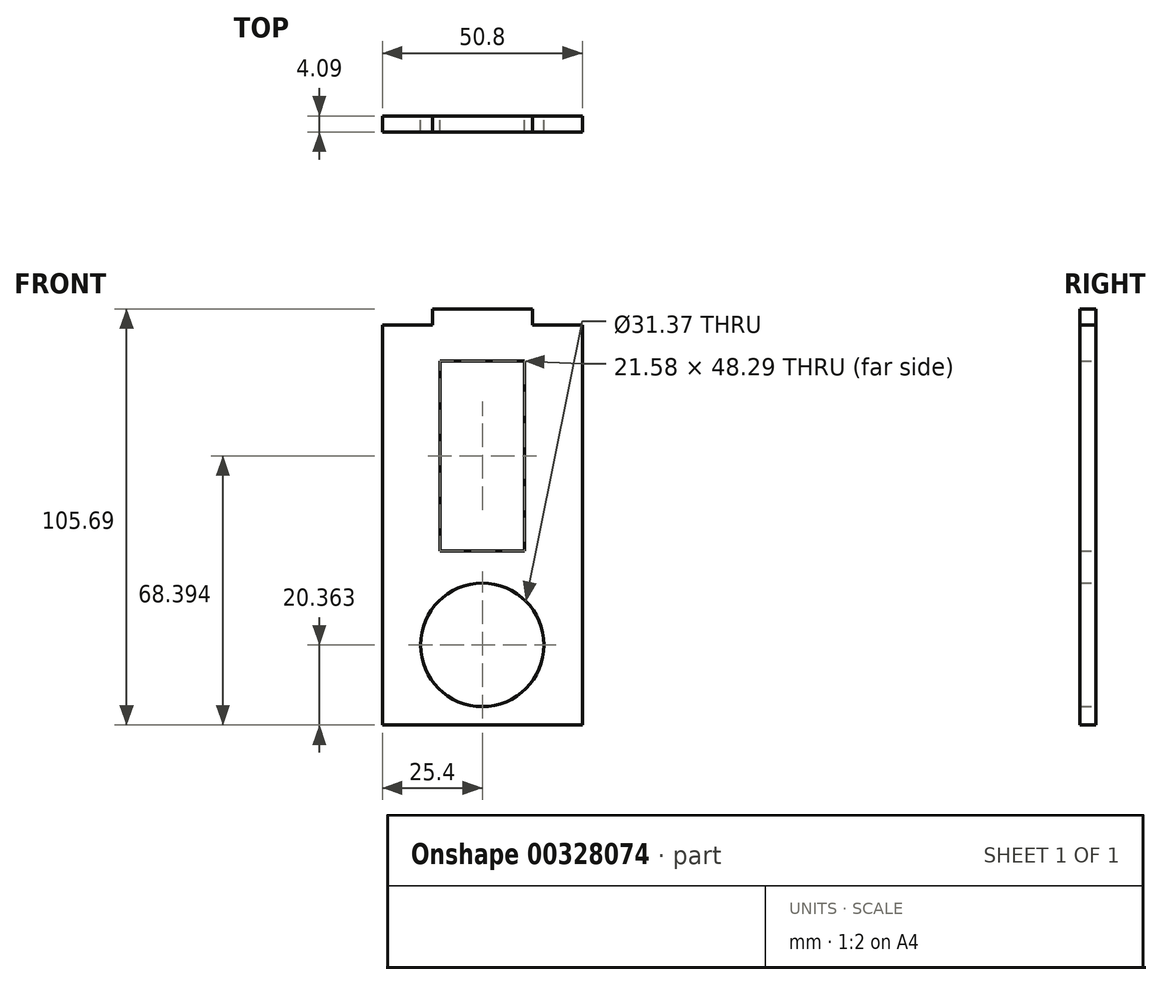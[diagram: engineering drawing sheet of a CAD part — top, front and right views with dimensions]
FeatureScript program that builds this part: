
annotation { "Feature Type Name" : "Feature", "Feature Type Description" : "" }
export const myFeature = defineFeature(function(context is Context, id is Id, definition is map)
    precondition{}
    {
        {
            var Q0;
            Q0=qCreatedBy(makeId("Front.planeOp"),FACE);
            var sketch = newSketch(context, id + "F0", { "sketchPlane" : qUnion([Q0])});
            skLineSegment(sketch, "E0.bottom", {"start": v(25.4, -50.8) * mm, "end": v(-25.4, -50.8) * mm});
            skLineSegment(sketch, "E0.top", {"start": v(25.4, 50.8) * mm, "end": v(-25.4, 50.8) * mm});
            skLineSegment(sketch, "E0.left", {"start": v(25.4, -50.8) * mm, "end": v(25.4, 50.8) * mm});
            skLineSegment(sketch, "E0.right", {"start": v(-25.4, -50.8) * mm, "end": v(-25.4, 50.8) * mm});
            skPoint(sketch, "E0.middle", {"position": v(0, 0) * mm});
            skCircle(sketch, "E1", {"center": v(0, -30.44) * mm, "radius": 15.68 * mm});
            skLineSegment(sketch, "E2", {"start": v(-25.4, -9.65) * mm, "end": v(25.4, -9.65) * mm, "construction": true});
            skLineSegment(sketch, "E3", {"start": v(0, -9.65) * mm, "end": v(0, 50.8) * mm, "construction": true});
            skLineSegment(sketch, "E4.top", {"start": v(12.7, 54.89) * mm, "end": v(-12.7, 54.89) * mm});
            skLineSegment(sketch, "E4.left", {"start": v(12.7, 50.8) * mm, "end": v(12.7, 54.89) * mm});
            skLineSegment(sketch, "E4.right", {"start": v(-12.7, 50.8) * mm, "end": v(-12.7, 54.89) * mm});
            skPoint(sketch, "E4.middle", {"position": v(0, 50.8) * mm});
            skPoint(sketch, "E5.orphan", {"position": v(-12.7, 46.71) * mm});
            skPoint(sketch, "E6.orphan", {"position": v(12.7, 46.71) * mm});
            skLineSegment(sketch, "E7.bottom", {"start": v(-10.79, -6.55) * mm, "end": v(10.79, -6.55) * mm});
            skLineSegment(sketch, "E7.top", {"start": v(-10.79, 41.74) * mm, "end": v(10.79, 41.74) * mm});
            skLineSegment(sketch, "E7.left", {"start": v(-10.79, -6.55) * mm, "end": v(-10.79, 41.74) * mm});
            skLineSegment(sketch, "E7.right", {"start": v(10.79, -6.55) * mm, "end": v(10.79, 41.74) * mm});
            skPoint(sketch, "E7.middle", {"position": v(0, 17.6) * mm});
            skSolve(sketch);
        }
        {
            var Q0;
            Q0 = qSketchRegion(id + "F0", true);
            extrude(context, id + "F1", {"entities" : qUnion([Q0]), "depth" : 4.1 * mm});
        }
    });
